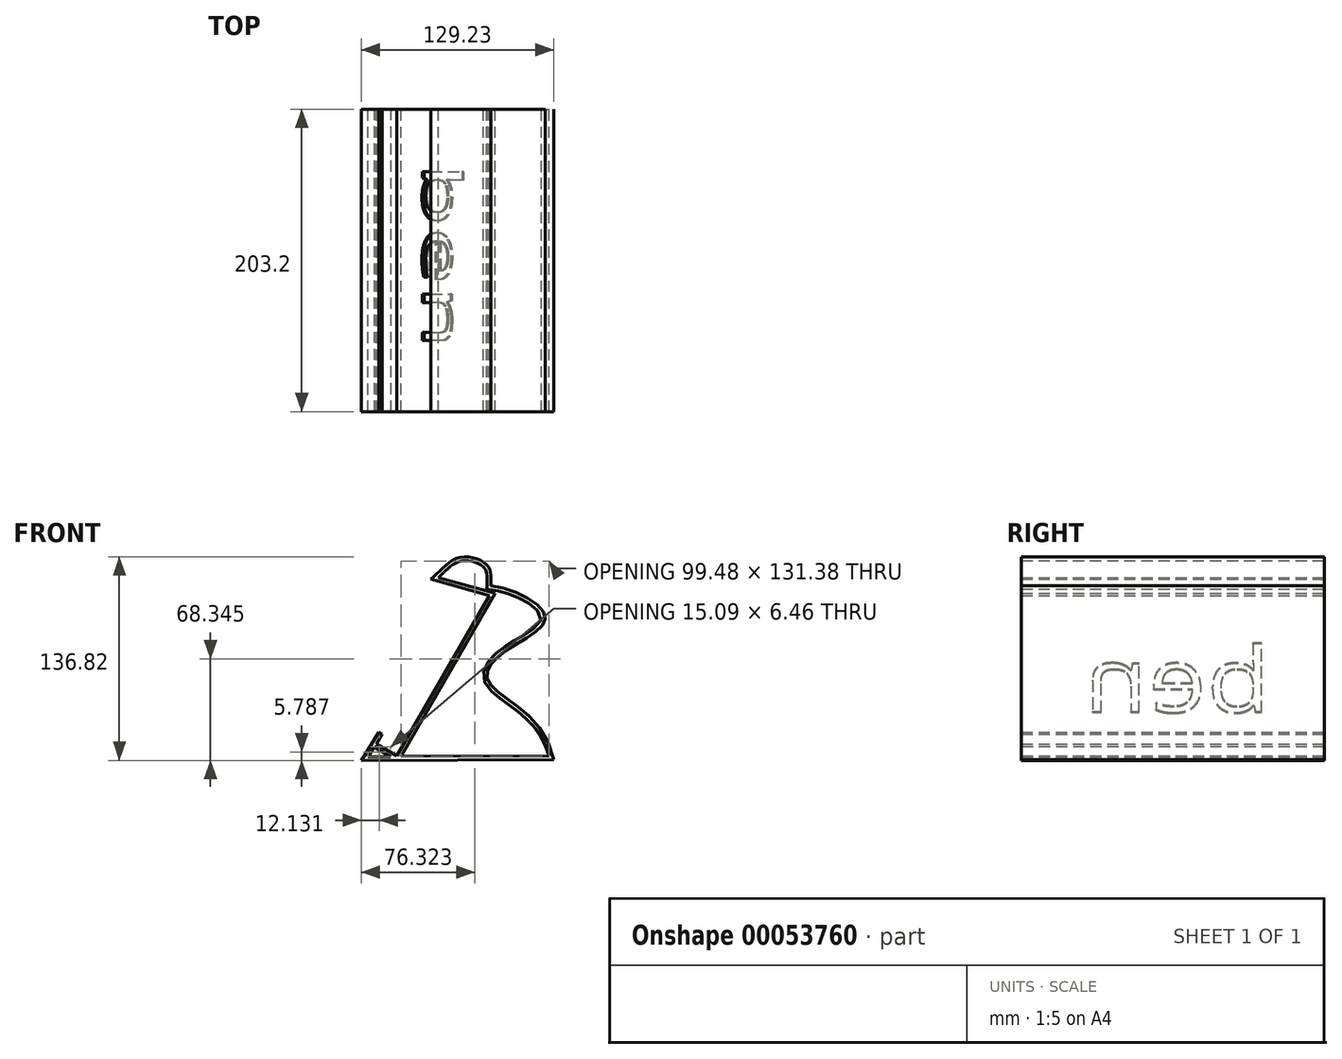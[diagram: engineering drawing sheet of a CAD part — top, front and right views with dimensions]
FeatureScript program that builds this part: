
annotation { "Feature Type Name" : "Feature", "Feature Type Description" : "" }
export const myFeature = defineFeature(function(context is Context, id is Id, definition is map)
    precondition{}
    {
        {
            var Q0;
            Q0=qCreatedBy(makeId("Front.planeOp"),FACE);
            var sketch = newSketch(context, id + "F0", { "sketchPlane" : qUnion([Q0])});
            skLineSegment(sketch, "E0.bottom", {"start": v(-48.07, 27.2) * mm, "end": v(28.13, 27.2) * mm, "construction": true});
            skLineSegment(sketch, "E0.top", {"start": v(-48.07, -60.38) * mm, "end": v(28.13, -60.38) * mm, "construction": true});
            skLineSegment(sketch, "E0.right", {"start": v(28.13, 27.2) * mm, "end": v(28.13, -60.38) * mm, "construction": true});
            skLineSegment(sketch, "E1", {"start": v(28.68, 49.29) * mm, "end": v(-33.55, -58.5) * mm});
            skLineSegment(sketch, "E2", {"start": v(-47.3, -50.56) * mm, "end": v(-43.49, -43.96) * mm});
            skLineSegment(sketch, "E3", {"start": v(-43.49, -43.96) * mm, "end": v(-45.69, -42.7) * mm});
            skLineSegment(sketch, "E4", {"start": v(-47.3, -50.56) * mm, "end": v(-33.55, -58.5) * mm});
            skLineSegment(sketch, "E5", {"start": v(-48.07, 27.2) * mm, "end": v(-48.07, -60.38) * mm, "construction": true});
            skPoint(sketch, "E6.1.internal.snap0", {"position": v(-9.97, -60.38) * mm});
            skLineSegment(sketch, "E7", {"start": v(-10.78, 60.11) * mm, "end": v(28.68, 49.29) * mm});
            skFitSpline(sketch, "E8", {"points": [v(-10.78, 60.11) * mm, v(7.85, 74.56) * mm, v(27.12, 69.41) * mm, v(29.44, 55.74) * mm], "startDerivative": vector(44.98, 35.08) * mm, "endDerivative": vector(-3.72, -58.28) * mm});
            skFitSpline(sketch, "E9", {"points": [v(29.44, 55.74) * mm, v(66.07, 34.13) * mm, v(37.42, 10.56) * mm, v(28.13, -9.1) * mm, v(71.77, -61.05) * mm], "startDerivative": vector(187.4, -19) * mm, "endDerivative": vector(57.6, -298.34) * mm});
            skLineSegment(sketch, "E10", {"start": v(-45.69, -42.7) * mm, "end": v(-57.46, -61.61) * mm});
            skLineSegment(sketch, "E11", {"start": v(-57.46, -61.61) * mm, "end": v(71.77, -61.05) * mm});
            skSolve(sketch);
        }
        {
            var Q0;
            Q0=qSketchRegion(id+"F0",true);
            extrude(context, id + "F1", {"entities" : qUnion([Q0]), "depth" : 203.2 * mm});
        }
        {
            var Q0;
            Q0=makeQuery(id+"F1.opExtrude","CAP_FACE",FACE,{"disambiguationData":[OSD([sQuery(id+"F0.wireOp",EDGE,"E1"),sQuery(id+"F0.wireOp",EDGE,"E2"),sQuery(id+"F0.wireOp",EDGE,"E3"),sQuery(id+"F0.wireOp",EDGE,"E4"),sQuery(id+"F0.wireOp",EDGE,"E7"),sQuery(id+"F0.wireOp",EDGE,"E8"),sQuery(id+"F0.wireOp",EDGE,"E9"),sQuery(id+"F0.wireOp",EDGE,"E10"),sQuery(id+"F0.wireOp",EDGE,"E11")])],"isStart":false});
            var Q1;
            Q1=makeQuery(id+"F1.opExtrude","CAP_FACE",FACE,{"disambiguationData":[OSD([sQuery(id+"F0.wireOp",EDGE,"E1"),sQuery(id+"F0.wireOp",EDGE,"E2"),sQuery(id+"F0.wireOp",EDGE,"E3"),sQuery(id+"F0.wireOp",EDGE,"E4"),sQuery(id+"F0.wireOp",EDGE,"E7"),sQuery(id+"F0.wireOp",EDGE,"E8"),sQuery(id+"F0.wireOp",EDGE,"E9"),sQuery(id+"F0.wireOp",EDGE,"E10"),sQuery(id+"F0.wireOp",EDGE,"E11")])],"isStart":true});
            shell(context, id + "F2", {"entities" : qUnion([Q0, Q1]), "thickness" : 2.54 * mm});
        }
        {
            var Q0;
            Q0=makeQuery(id+"F1.opExtrude","SWEPT_FACE",FACE,{"disambiguationData":[OSD([sQuery(id+"F0.wireOp",EDGE,"E1")])]});
            var sketch = newSketch(context, id + "F3", { "sketchPlane" : qUnion([Q0])});
            skText(sketch, "E12", { "text": "ben", "fontName": "OpenSans-Regular.ttf"});
            const initialGuessF3  = {"E12": [0.03597, -0.03314, 1, 0, 0.0504]};
            skSetInitialGuess(sketch, initialGuessF3);
            skSolve(sketch);
        }
        {
            var Q0;
            Q0=qSketchRegion(id+"F3",true);
            extrude(context, id + "F4", {"entities" : qUnion([Q0]), "operationType" : NewBodyOperationType.REMOVE, "oppositeDirection" : true, "depth" : 1.27 * mm});
        }
    });
